# Revit family: FC-185-19-1
name_source: partatom
category: Aparatos sanitarios
units: mm (PartAtom-declared; Revit-internal decimal feet)

## family parameters
Compartido = Sí
Corte con vacíos al cargar = No
Cota de conector redondo = Diámetro de uso
Número OmniClass = 23.45.00.00
Punto de cálculo de habitación = No
Se basa en plano de trabajo = No
Siempre vertical = Sí
Tipo de pieza = Normal
Título OmniClass = Sanitary, Laundry, and Cleaning Equipment

## types (1)
- FC-185-19-1
    Chrome = Brass Chromed
    Comentarios de tipo = Flushvalves
    Compliance = NOM-005-CONAGUA-1996
    Conexión AF = Sí
    Connection = 1" Feeding Connection
    Descripción = ¾" Sensor Flushvalve Ac Powered With Manual Flush Button
    Detection Range = 0 - 15.74"
    Elevación por defecto = 0"
    Fabricante = Helvex
    Features = Operates With a 6 Vc Power Supply; Manual Flush Button; Antibacterial Coating Manual Flush Button; Left or Right Connection
    Feeding Voltage = 6 V
    Flow = 0.26 Gallons Per Flush
    Max. Working Pressure = 85.3 psi
    Min. Working Pressure = 14.2 psi
    Modelo = FC-185-19-1
    Note = Feeding Pipe Must Be 1 ¼" and Connect a 1 ¼" - 1" Reductor to Stop Valve

## geometry (parser evidence)
native form markers: Sweep x3
no freeform markers — native parametric forms only
